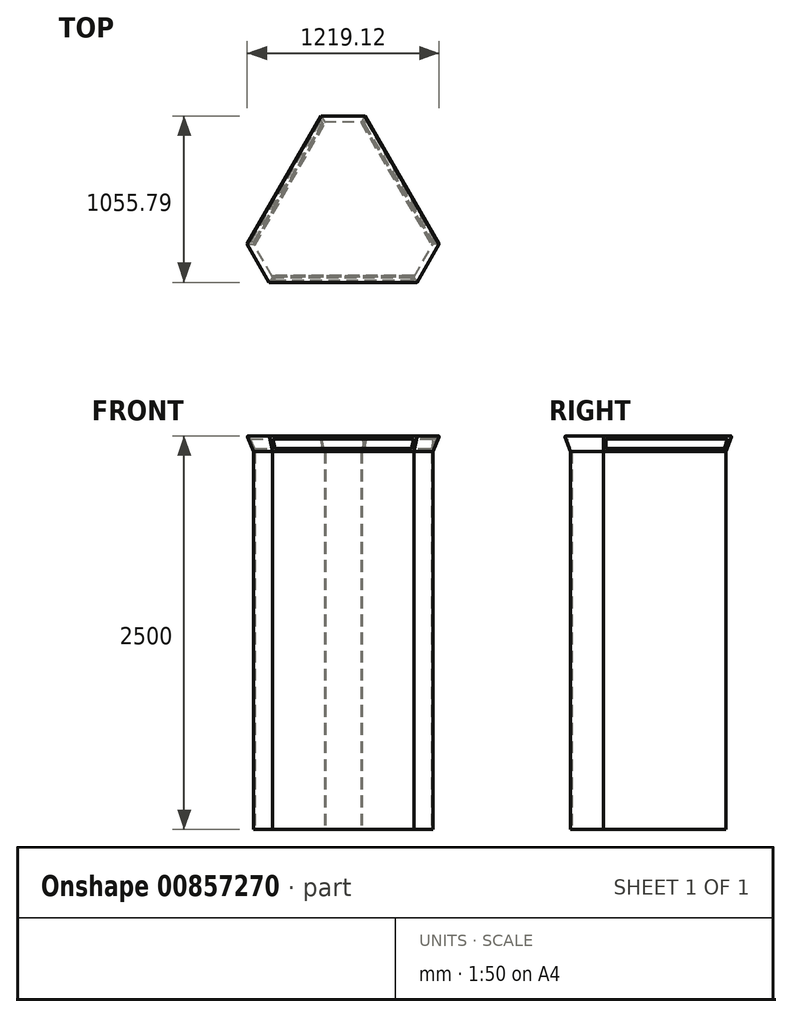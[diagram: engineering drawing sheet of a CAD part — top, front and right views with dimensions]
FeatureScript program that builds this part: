
annotation { "Feature Type Name" : "Feature", "Feature Type Description" : "" }
export const myFeature = defineFeature(function(context is Context, id is Id, definition is map)
    precondition{}
    {
        {
            var Q0;
            Q0=qCreatedBy(makeId("Top.planeOp"),FACE);
            var sketch = newSketch(context, id + "F0", { "sketchPlane" : qUnion([Q0])});
            skLineSegment(sketch, "E0", {"start": v(-570, 207.85) * mm, "end": v(-120, 987.27) * mm});
            skLineSegment(sketch, "E1", {"start": v(120, 987.27) * mm, "end": v(570, 207.85) * mm});
            skLineSegment(sketch, "E2", {"start": v(-450, 0) * mm, "end": v(450, 0) * mm});
            skLineSegment(sketch, "E3", {"start": v(-690, 0) * mm, "end": v(345, 597.56) * mm, "construction": true});
            skLineSegment(sketch, "E4", {"start": v(690, 0) * mm, "end": v(-345, 597.56) * mm, "construction": true});
            skLineSegment(sketch, "E5", {"start": v(0, 1195.12) * mm, "end": v(0, 0) * mm, "construction": true});
            skLineSegment(sketch, "E6", {"start": v(-120, 987.27) * mm, "end": v(120, 987.27) * mm});
            skLineSegment(sketch, "E7", {"start": v(-450, 0) * mm, "end": v(-570, 207.85) * mm});
            skLineSegment(sketch, "E8", {"start": v(450, 0) * mm, "end": v(570, 207.85) * mm});
            skSolve(sketch);
        }
        {
            var Q0;
            Q0=qSketchRegion(id+"F0",true);
            extrude(context, id + "F1", {"entities" : qUnion([Q0]), "depth" : 2400 * mm, "offsetDistance" : 25 * mm});
        }
        {
            var Q0;
            Q0=makeQuery(id+"F1.opExtrude","CAP_FACE",FACE,{"disambiguationData":[OSD([sQuery(id+"F0.wireOp",EDGE,"E0"),sQuery(id+"F0.wireOp",EDGE,"E1"),sQuery(id+"F0.wireOp",EDGE,"E2"),sQuery(id+"F0.wireOp",EDGE,"E6"),sQuery(id+"F0.wireOp",EDGE,"E7"),sQuery(id+"F0.wireOp",EDGE,"E8")])],"isStart":false});
            var sketch = newSketch(context, id + "F2", { "sketchPlane" : qUnion([Q0])});
            skLineSegment(sketch, "E9.0", {"start": v(-350, 40) * mm, "end": v(350, 40) * mm});
            skLineSegment(sketch, "E10.0", {"start": v(-485.36, 274.45) * mm, "end": v(-135.36, 880.67) * mm});
            skLineSegment(sketch, "E11", {"start": v(-350, 40) * mm, "end": v(-350, 90) * mm});
            skLineSegment(sketch, "E12", {"start": v(-350, 90) * mm, "end": v(350, 90) * mm});
            skLineSegment(sketch, "E13", {"start": v(350, 90) * mm, "end": v(350, 40) * mm});
            skLineSegment(sketch, "E14", {"start": v(-135.36, 880.67) * mm, "end": v(-92.06, 855.67) * mm});
            skLineSegment(sketch, "E15", {"start": v(-92.06, 855.67) * mm, "end": v(-442.06, 249.45) * mm});
            skLineSegment(sketch, "E16", {"start": v(-442.06, 249.45) * mm, "end": v(-485.36, 274.45) * mm});
            skLineSegment(sketch, "E17", {"start": v(-345, 597.56) * mm, "end": v(-140.02, 479.21) * mm, "construction": true});
            skLineSegment(sketch, "E18", {"start": v(0, 0) * mm, "end": v(0, 987.27) * mm, "construction": true});
            skLineSegment(sketch, "E19.MirrorCS", {"start": v(-92.06, 855.67) * mm, "end": v(-135.36, 880.67) * mm});
            skLineSegment(sketch, "E20.MirrorCS", {"start": v(-485.36, 274.45) * mm, "end": v(-442.06, 249.45) * mm});
            skLineSegment(sketch, "E21.MirrorCS", {"start": v(-135.36, 880.67) * mm, "end": v(-485.36, 274.45) * mm});
            skLineSegment(sketch, "E22.MirrorCS", {"start": v(-442.06, 249.45) * mm, "end": v(-92.06, 855.67) * mm});
            skLineSegment(sketch, "E23.MirrorCS", {"start": v(135.36, 880.67) * mm, "end": v(92.06, 855.67) * mm});
            skLineSegment(sketch, "E24.MirrorCS", {"start": v(442.06, 249.45) * mm, "end": v(485.36, 274.45) * mm});
            skLineSegment(sketch, "E25.MirrorCS", {"start": v(485.36, 274.45) * mm, "end": v(442.06, 249.45) * mm});
            skLineSegment(sketch, "E26.MirrorCS", {"start": v(92.06, 855.67) * mm, "end": v(135.36, 880.67) * mm});
            skLineSegment(sketch, "E27.MirrorCS", {"start": v(92.06, 855.67) * mm, "end": v(442.06, 249.45) * mm});
            skLineSegment(sketch, "E28.MirrorCS", {"start": v(485.36, 274.45) * mm, "end": v(135.36, 880.67) * mm});
            skLineSegment(sketch, "E29.MirrorCS", {"start": v(135.36, 880.67) * mm, "end": v(485.36, 274.45) * mm});
            skLineSegment(sketch, "E30.MirrorCS", {"start": v(442.06, 249.45) * mm, "end": v(92.06, 855.67) * mm});
            skSolve(sketch);
        }
        {
            var Q0;
            Q0=qCreatedBy(makeId("Right.planeOp"),FACE);
            var sketch = newSketch(context, id + "F3", { "sketchPlane" : qUnion([Q0])});
            skPoint(sketch, "E31.2", {"position": v(103.92, 2400) * mm});
            skLineSegment(sketch, "E32", {"start": v(398.37, 2400) * mm, "end": v(398.37, -119.7) * mm, "construction": true});
            skPoint(sketch, "E32.endSnap0", {"position": v(398.37, 2400) * mm});
            skSolve(sketch);
        }
        {
            var Q0;
            Q0=makeQuery(id+"F1.opExtrude","CAP_FACE",FACE,{"disambiguationData":[OSD([sQuery(id+"F0.wireOp",EDGE,"E0"),sQuery(id+"F0.wireOp",EDGE,"E1"),sQuery(id+"F0.wireOp",EDGE,"E2"),sQuery(id+"F0.wireOp",EDGE,"E6"),sQuery(id+"F0.wireOp",EDGE,"E7"),sQuery(id+"F0.wireOp",EDGE,"E8")])],"isStart":true});
            var sketch = newSketch(context, id + "F4", { "sketchPlane" : qUnion([Q0])});
            skLineSegment(sketch, "E33.0", {"start": v(-570, -207.85) * mm, "end": v(-120, -987.27) * mm});
            skLineSegment(sketch, "E33.1", {"start": v(120, -987.27) * mm, "end": v(570, -207.85) * mm});
            skLineSegment(sketch, "E33.2", {"start": v(-450, 0) * mm, "end": v(450, 0) * mm});
            skLineSegment(sketch, "E34.0", {"start": v(-561.34, -202.85) * mm, "end": v(-111.34, -982.27) * mm});
            skLineSegment(sketch, "E35.0", {"start": v(-450, -10) * mm, "end": v(450, -10) * mm});
            skLineSegment(sketch, "E36.0", {"start": v(111.34, -982.27) * mm, "end": v(561.34, -202.85) * mm});
            skLineSegment(sketch, "E37", {"start": v(-111.34, -982.27) * mm, "end": v(-120, -987.27) * mm});
            skLineSegment(sketch, "E38", {"start": v(-570, -207.85) * mm, "end": v(-561.34, -202.85) * mm});
            skLineSegment(sketch, "E39", {"start": v(-450, 0) * mm, "end": v(-450, -10) * mm});
            skLineSegment(sketch, "E40", {"start": v(450, 0) * mm, "end": v(450, -10) * mm});
            skLineSegment(sketch, "E41", {"start": v(570, -207.85) * mm, "end": v(561.34, -202.85) * mm});
            skLineSegment(sketch, "E42", {"start": v(120, -987.27) * mm, "end": v(111.34, -982.27) * mm});
            skSolve(sketch);
        }
        {
            var Q0;
            Q0=qSketchRegion(id+"F4",true);
            var Q1;
            Q1=makeQuery(id+"F1.opExtrude","CAP_FACE",FACE,{"disambiguationData":[OSD([sQuery(id+"F0.wireOp",EDGE,"E0"),sQuery(id+"F0.wireOp",EDGE,"E1"),sQuery(id+"F0.wireOp",EDGE,"E2"),sQuery(id+"F0.wireOp",EDGE,"E6"),sQuery(id+"F0.wireOp",EDGE,"E7"),sQuery(id+"F0.wireOp",EDGE,"E8")])],"isStart":false});
            extrude(context, id + "F5", {"entities" : qUnion([Q0]), "operationType" : NewBodyOperationType.REMOVE, "endBound" : BoundingType.UP_TO_SURFACE, "oppositeDirection" : true, "depth" : 25 * mm, "endBoundEntityFace" : qUnion([Q1]), "offsetDistance" : 25 * mm});
        }
        {
            var Q0;
            Q0=makeQuery(id+"F1.opExtrude","CAP_FACE",FACE,{"disambiguationData":[OSD([sQuery(id+"F0.wireOp",EDGE,"E0"),sQuery(id+"F0.wireOp",EDGE,"E1"),sQuery(id+"F0.wireOp",EDGE,"E2"),sQuery(id+"F0.wireOp",EDGE,"E6"),sQuery(id+"F0.wireOp",EDGE,"E7"),sQuery(id+"F0.wireOp",EDGE,"E8")])],"isStart":true});
            var sketch = newSketch(context, id + "F6", { "sketchPlane" : qUnion([Q0])});
            skLineSegment(sketch, "E43.0", {"start": v(-560.84, -203.71) * mm, "end": v(-111.84, -981.4) * mm});
            skLineSegment(sketch, "E44.0", {"start": v(-569.5, -208.71) * mm, "end": v(-120.5, -986.4) * mm});
            skLineSegment(sketch, "E45.0", {"start": v(-111.84, -981.4) * mm, "end": v(-120.5, -986.4) * mm});
            skLineSegment(sketch, "E46.0", {"start": v(-569.5, -208.71) * mm, "end": v(-560.84, -203.71) * mm});
            skPoint(sketch, "E47.orphan", {"position": v(-561.34, -202.85) * mm});
            skPoint(sketch, "E48.orphan", {"position": v(-111.34, -982.27) * mm});
            skSolve(sketch);
        }
        {
            var Q0;
            Q0=qSketchRegion(id+"F6",true);
            var Q1;
            Q1=makeQuery(id+"F1.opExtrude","CAP_FACE",FACE,{"disambiguationData":[OSD([sQuery(id+"F0.wireOp",EDGE,"E0"),sQuery(id+"F0.wireOp",EDGE,"E1"),sQuery(id+"F0.wireOp",EDGE,"E2"),sQuery(id+"F0.wireOp",EDGE,"E6"),sQuery(id+"F0.wireOp",EDGE,"E7"),sQuery(id+"F0.wireOp",EDGE,"E8")])],"isStart":false});
            extrude(context, id + "F7", {"entities" : qUnion([Q0]), "endBound" : BoundingType.UP_TO_SURFACE, "oppositeDirection" : true, "depth" : 25 * mm, "endBoundEntityFace" : qUnion([Q1]), "offsetDistance" : 25 * mm});
        }
        {
            var Q0;
            Q0=makeQuery(id+"F7.opExtrude","SWEPT_BODY",BODY,{"disambiguationData":[OSD([sQuery(id+"F6.wireOp",EDGE,"E43.0"),sQuery(id+"F6.wireOp",EDGE,"E44.0"),sQuery(id+"F6.wireOp",EDGE,"E45.0"),sQuery(id+"F6.wireOp",EDGE,"E46.0")])]});
            var Q1;
            Q1=sQuery(id+"F3.wireOp",EDGE,"E32");
            circularPattern(context, id + "F8", {"entities" : qUnion([Q0]), "axis" : qUnion([Q1]), "angle" : 360 * degree, "instanceCount" : 3, "equalSpace" : true});
        }
        {
            var Q0;
            Q0=makeQuery(id+"F1.opExtrude","SWEPT_FACE",FACE,{"disambiguationData":[OSD([sQuery(id+"F0.wireOp",EDGE,"E7")])]});
            var Q1;
            Q1=makeQuery(id+"F7.opExtrude","SWEPT_EDGE",EDGE,{"disambiguationData":[OSD([sQuery(id+"F6.wireOp",EDGE,"E44.0"),sQuery(id+"F6.wireOp",EDGE,"E46.0")])]});
            cPlane(context, id + "F9", {"entities" : qUnion([Q0, Q1]), "cplaneType" : CPlaneType.LINE_ANGLE, "offset" : 25 * mm, "angle" : 90 * degree, "width" : 150 * mm, "height" : 150 * mm});
        }
        {
            var Q0;
            Q0=qCreatedBy(id+"F9.planeOp",FACE);
            cPlane(context, id + "F10", {"entities" : qUnion([Q0]), "cplaneType" : CPlaneType.OFFSET, "offset" : 120.5 * mm, "width" : 150 * mm, "height" : 150 * mm});
        }
        {
            var Q0;
            Q0=makeQuery(id+"F1.opExtrude","CAP_FACE",FACE,{"disambiguationData":[OSD([sQuery(id+"F0.wireOp",EDGE,"E0"),sQuery(id+"F0.wireOp",EDGE,"E1"),sQuery(id+"F0.wireOp",EDGE,"E2"),sQuery(id+"F0.wireOp",EDGE,"E6"),sQuery(id+"F0.wireOp",EDGE,"E7"),sQuery(id+"F0.wireOp",EDGE,"E8")])],"isStart":false});
            var sketch = newSketch(context, id + "F11", { "sketchPlane" : qUnion([Q0])});
            skLineSegment(sketch, "E49.0", {"start": v(450, 0) * mm, "end": v(570, 207.85) * mm});
            skLineSegment(sketch, "E49.1", {"start": v(-450, 0) * mm, "end": v(-570, 207.85) * mm});
            skLineSegment(sketch, "E49.2", {"start": v(-120, 987.27) * mm, "end": v(120, 987.27) * mm});
            skLineSegment(sketch, "E50", {"start": v(-570, 207.85) * mm, "end": v(-120, 987.27) * mm});
            skLineSegment(sketch, "E51", {"start": v(-450, 0) * mm, "end": v(450, 0) * mm});
            skLineSegment(sketch, "E52", {"start": v(570, 207.85) * mm, "end": v(120, 987.27) * mm});
            skSolve(sketch);
        }
        {
            var Q0;
            Q0 = qSketchRegion(id + "F11", true);
            extrude(context, id + "F12", {"entities" : qUnion([Q0]), "depth" : 100 * mm, "offsetDistance" : 25 * mm, "hasDraft" : true, "draftAngle" : 20 * degree});
        }
        {
            var Q0;
            Q0=makeQuery(id+"F8.opPattern","COPY",FACE,{"derivedFrom":makeQuery(id+"F7.opExtrude","SWEPT_FACE",FACE,{"disambiguationData":[OSD([sQuery(id+"F6.wireOp",EDGE,"E44.0")])]}),"instanceName":"1"});
            var sketch = newSketch(context, id + "F13", { "sketchPlane" : qUnion([Q0])});
            skLineSegment(sketch, "E53.0", {"start": v(-126.01, 2500) * mm, "end": v(-105, 2400) * mm, "construction": true});
            skLineSegment(sketch, "E54.0", {"start": v(-126.01, 2500) * mm, "end": v(816.01, 2500) * mm, "construction": true});
            skLineSegment(sketch, "E55.0", {"start": v(816.01, 2500) * mm, "end": v(795, 2400) * mm, "construction": true});
            skLineSegment(sketch, "E56.0", {"start": v(794, 2400) * mm, "end": v(-104, 2400) * mm, "construction": true});
            skLineSegment(sketch, "E57.0", {"start": v(778.77, 2420) * mm, "end": v(-88.77, 2420) * mm});
            skLineSegment(sketch, "E58.trimOffspring", {"start": v(-101.37, 2480) * mm, "end": v(-88.77, 2420) * mm});
            skLineSegment(sketch, "E59.trimOffspring", {"start": v(-101.37, 2480) * mm, "end": v(791.37, 2480) * mm});
            skLineSegment(sketch, "E60.trimOffspring", {"start": v(791.37, 2480) * mm, "end": v(778.77, 2420) * mm});
            skSolve(sketch);
        }
        {
            var Q0;
            Q0 = qSketchRegion(id + "F13", true);
            extrude(context, id + "F14", {"entities" : qUnion([Q0]), "operationType" : NewBodyOperationType.REMOVE, "depth" : 40 * mm, "offsetDistance" : 25 * mm});
        }
        {
            var Q0;
            Q0=makeQuery(id+"F14.boolean.opBoolean","COPY",EDGE,{"derivedFrom":makeQuery(id+"F14.opExtrude","SWEPT_EDGE",EDGE,{"disambiguationData":[OSD([sQuery(id+"F13.wireOp",EDGE,"E58.trimOffspring"),sQuery(id+"F13.wireOp",EDGE,"E59.trimOffspring")])]})});
            var Q1;
            Q1=makeQuery(id+"F14.boolean.opBoolean","COPY",EDGE,{"derivedFrom":makeQuery(id+"F14.opExtrude","SWEPT_EDGE",EDGE,{"disambiguationData":[OSD([sQuery(id+"F13.wireOp",EDGE,"E57.0"),sQuery(id+"F13.wireOp",EDGE,"E58.trimOffspring")])]})});
            var Q2;
            Q2=makeQuery(id+"F14.boolean.opBoolean","COPY",EDGE,{"derivedFrom":makeQuery(id+"F14.opExtrude","SWEPT_EDGE",EDGE,{"disambiguationData":[OSD([sQuery(id+"F13.wireOp",EDGE,"E59.trimOffspring"),sQuery(id+"F13.wireOp",EDGE,"E60.trimOffspring")])]})});
            var Q3;
            Q3=makeQuery(id+"F14.boolean.opBoolean","COPY",EDGE,{"derivedFrom":makeQuery(id+"F14.opExtrude","SWEPT_EDGE",EDGE,{"disambiguationData":[OSD([sQuery(id+"F13.wireOp",EDGE,"E57.0"),sQuery(id+"F13.wireOp",EDGE,"E60.trimOffspring")])]})});
            fillet(context, id + "F15", {"entities" : qUnion([Q0, Q1, Q2, Q3]), "radius" : 5 * mm, "tangentPropagation" : true, "allowEdgeOverflow" : false});
        }
        {
            var Q0;
            Q0=qCreatedBy(id+"F10.planeOp",FACE);
            var sketch = newSketch(context, id + "F16", { "sketchPlane" : qUnion([Q0])});
            skLineSegment(sketch, "E61.0", {"start": v(626.68, 2480) * mm, "end": v(604.84, 2420) * mm});
            skLineSegment(sketch, "E61.1", {"start": v(604.84, 2420) * mm, "end": v(597.56, 2420) * mm});
            skLineSegment(sketch, "E62", {"start": v(597.56, 2420) * mm, "end": v(619.4, 2480) * mm});
            skLineSegment(sketch, "E63.0", {"start": v(626.68, 2480) * mm, "end": v(619.4, 2480) * mm});
            skPoint(sketch, "E64.orphan", {"position": v(597.56, 2480) * mm});
            skSolve(sketch);
        }
        {
            var Q0;
            Q0 = qSketchRegion(id + "F16", true);
            var Q1;
            Q1=makeQuery(id+"F14.boolean.opBoolean","COPY",FACE,{"derivedFrom":makeQuery(id+"F14.opExtrude","SWEPT_FACE",FACE,{"disambiguationData":[OSD([sQuery(id+"F13.wireOp",EDGE,"E60.trimOffspring")])]})});
            var Q2;
            Q2=makeQuery(id+"F14.boolean.opBoolean","COPY",FACE,{"derivedFrom":makeQuery(id+"F14.opExtrude","SWEPT_FACE",FACE,{"disambiguationData":[OSD([sQuery(id+"F13.wireOp",EDGE,"E58.trimOffspring")])]})});
            extrude(context, id + "F17", {"entities" : qUnion([Q0]), "endBound" : BoundingType.UP_TO_SURFACE, "oppositeDirection" : true, "depth" : 25 * mm, "endBoundEntityFace" : qUnion([Q1]), "offsetDistance" : 25 * mm, "hasSecondDirection" : true, "secondDirectionBound" : BoundingType.UP_TO_SURFACE, "secondDirectionOppositeDirection" : false, "secondDirectionDepth" : 25 * mm, "secondDirectionBoundEntityFace" : qUnion([Q2])});
        }
        {
            var Q0;
            Q0=makeQuery(id+"F17.opExtrude","CAP_EDGE",EDGE,{"disambiguationData":[OSD([sQuery(id+"F16.wireOp",EDGE,"E63.0")]),topologyDisambiguationEdgeConnected([makeQuery(id+"F14.boolean.opBoolean","COPY",FACE,{"derivedFrom":makeQuery(id+"F14.opExtrude","SWEPT_FACE",FACE,{"disambiguationData":[OSD([sQuery(id+"F13.wireOp",EDGE,"E58.trimOffspring")])]})})])],"isStart":false});
            var Q1;
            Q1=makeQuery(id+"F17.opExtrude","CAP_EDGE",EDGE,{"disambiguationData":[OSD([sQuery(id+"F16.wireOp",EDGE,"E61.1")]),topologyDisambiguationEdgeConnected([makeQuery(id+"F14.boolean.opBoolean","COPY",FACE,{"derivedFrom":makeQuery(id+"F14.opExtrude","SWEPT_FACE",FACE,{"disambiguationData":[OSD([sQuery(id+"F13.wireOp",EDGE,"E58.trimOffspring")])]})})])],"isStart":false});
            var Q2;
            Q2=makeQuery(id+"F17.opExtrude","CAP_EDGE",EDGE,{"disambiguationData":[OSD([sQuery(id+"F16.wireOp",EDGE,"E63.0")]),topologyDisambiguationEdgeConnected([makeQuery(id+"F14.boolean.opBoolean","COPY",FACE,{"derivedFrom":makeQuery(id+"F14.opExtrude","SWEPT_FACE",FACE,{"disambiguationData":[OSD([sQuery(id+"F13.wireOp",EDGE,"E60.trimOffspring")])]})})])],"isStart":false});
            var Q3;
            Q3=makeQuery(id+"F17.opExtrude","CAP_EDGE",EDGE,{"disambiguationData":[OSD([sQuery(id+"F16.wireOp",EDGE,"E61.1")]),topologyDisambiguationEdgeConnected([makeQuery(id+"F14.boolean.opBoolean","COPY",FACE,{"derivedFrom":makeQuery(id+"F14.opExtrude","SWEPT_FACE",FACE,{"disambiguationData":[OSD([sQuery(id+"F13.wireOp",EDGE,"E60.trimOffspring")])]})})])],"isStart":false});
            fillet(context, id + "F18", {"entities" : qUnion([Q0, Q1, Q2, Q3]), "radius" : 5 * mm, "tangentPropagation" : true, "allowEdgeOverflow" : false});
        }
        {
            var Q0;
            Q0=makeQuery(id+"F17.opExtrude","SWEPT_BODY",BODY,{"disambiguationData":[OSD([sQuery(id+"F16.wireOp",EDGE,"E61.0"),sQuery(id+"F16.wireOp",EDGE,"E61.1"),sQuery(id+"F16.wireOp",EDGE,"E62"),sQuery(id+"F16.wireOp",EDGE,"E63.0")])]});
            var Q1;
            Q1=sQuery(id+"F3.wireOp",EDGE,"E32");
            circularPattern(context, id + "F19", {"entities" : qUnion([Q0]), "axis" : qUnion([Q1]), "angle" : 360 * degree, "instanceCount" : 3, "equalSpace" : true});
        }
        {
            var Q0;
            Q0=makeQuery(id+"F12.opExtrude","CAP_EDGE",EDGE,{"disambiguationData":[OSD([sQuery(id+"F11.wireOp",EDGE,"E49.0")])],"isStart":false});
            var Q1;
            Q1=makeQuery(id+"F12.opExtrude","CAP_EDGE",EDGE,{"disambiguationData":[OSD([sQuery(id+"F11.wireOp",EDGE,"E52")])],"isStart":false});
            var Q2;
            Q2=makeQuery(id+"F12.opExtrude","CAP_EDGE",EDGE,{"disambiguationData":[OSD([sQuery(id+"F11.wireOp",EDGE,"E49.2")])],"isStart":false});
            var Q3;
            Q3=makeQuery(id+"F12.opExtrude","CAP_EDGE",EDGE,{"disambiguationData":[OSD([sQuery(id+"F11.wireOp",EDGE,"E50")])],"isStart":false});
            var Q4;
            Q4=makeQuery(id+"F12.opExtrude","CAP_EDGE",EDGE,{"disambiguationData":[OSD([sQuery(id+"F11.wireOp",EDGE,"E51")])],"isStart":false});
            var Q5;
            Q5=makeQuery(id+"F12.opExtrude","CAP_EDGE",EDGE,{"disambiguationData":[OSD([sQuery(id+"F11.wireOp",EDGE,"E49.1")])],"isStart":false});
            fillet(context, id + "F20", {"entities" : qUnion([Q0, Q1, Q2, Q3, Q4, Q5]), "radius" : 5 * mm, "tangentPropagation" : true, "allowEdgeOverflow" : false});
        }
    });
